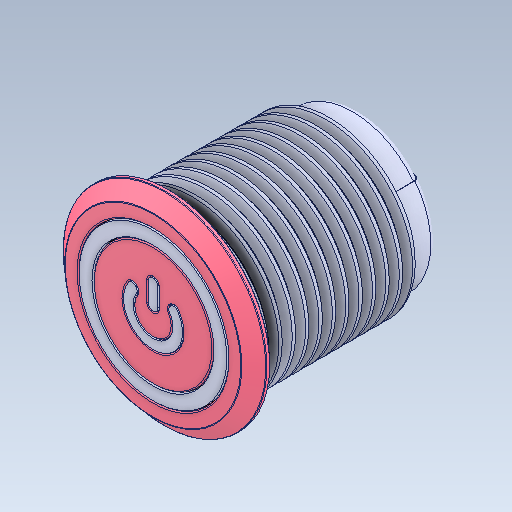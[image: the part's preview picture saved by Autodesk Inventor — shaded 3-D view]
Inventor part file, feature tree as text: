
AUTODESK INVENTOR PART (.ipt)
format: ipt  version: 2020 (Build 240168000, 168)  size: 602,112 bytes
history: mixed  units: mm
features: other x7, fillet x1, imported_body x1
ambient origin geometry x8: Origin, YZ Plane, XZ Plane, XY Plane, X Axis, Y Axis, Z Axis, Center Point
bodies: Body1 (imported_parasolid), Body2 (imported_parasolid), Body3 (imported_parasolid), Body4 (imported_parasolid)
feature tree (9):
  other  "Bryła1"
  other  "Bryła2"
  other  "Bryła3"
  other  "Bryła4"
  other  "Boss-Extrude4"
  other  "Boss-Extrude6"
  other  "Boss-Extrude7"
  fillet  "Fillet3"  [1 undecoded]
  imported_body  NMx_Import_Brep_tag  [imported B-rep: ~23 faces, bbox_mm=[8.494201, 1.52349, 0.5]]
note: 1 required parameter value undecoded (feature->parameter linkage not recoverable at this tier; creation-order binding heuristic only, values carry confidence <= 0.55)
